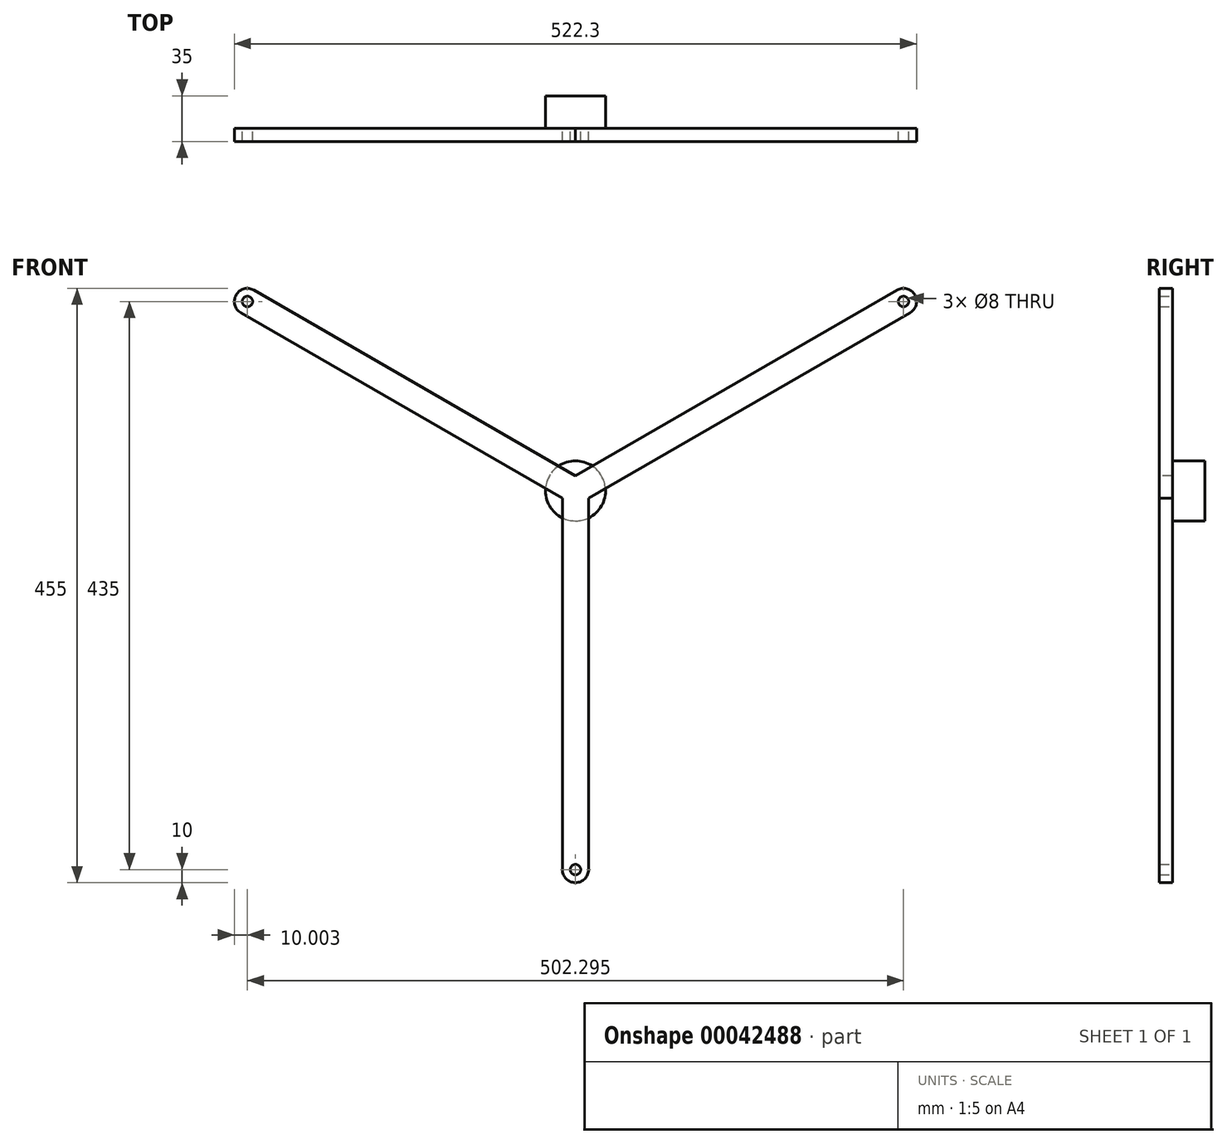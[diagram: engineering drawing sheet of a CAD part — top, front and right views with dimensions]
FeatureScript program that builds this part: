
annotation { "Feature Type Name" : "Feature", "Feature Type Description" : "" }
export const myFeature = defineFeature(function(context is Context, id is Id, definition is map)
    precondition{}
    {
        {
            var Q0;
            Q0=qCreatedBy(makeId("Front.planeOp"),FACE);
            var sketch = newSketch(context, id + "F0", { "sketchPlane" : qUnion([Q0])});
            skLineSegment(sketch, "E0.bottom", {"start": v(0, -300) * mm, "end": v(0, -300) * mm});
            skLineSegment(sketch, "E0.top", {"start": v(-10, 0) * mm, "end": v(10, 0) * mm});
            skLineSegment(sketch, "E0.left", {"start": v(-10, -290) * mm, "end": v(-10, 0) * mm});
            skLineSegment(sketch, "E0.right", {"start": v(10, -290) * mm, "end": v(10, 0) * mm});
            skCircle(sketch, "E1", {"center": v(0, -290) * mm, "radius": 4 * mm});
            skPoint(sketch, "E2.visualSharp", {"position": v(10, -300) * mm});
            skArc(sketch, "E2.filletArc", {"start": v(0, -300) * mm, "mid": v(7.07, -297.07) * mm, "end": v(10, -290) * mm});
            skPoint(sketch, "E3.visualSharp", {"position": v(-10, -300) * mm});
            skArc(sketch, "E3.filletArc", {"start": v(-10, -290) * mm, "mid": v(-7.07, -297.07) * mm, "end": v(0, -300) * mm});
            skSolve(sketch);
        }
        {
            var Q0;
            Q0 = qSketchRegion(id + "F0", true);
            extrude(context, id + "F1", {"entities" : qUnion([Q0]), "depth" : 10 * mm});
        }
        {
            var Q0;
            Q0=qCreatedBy(makeId("Right.planeOp"),FACE);
            var sketch = newSketch(context, id + "F2", { "sketchPlane" : qUnion([Q0])});
            skLineSegment(sketch, "E4", {"start": v(0, 0) * mm, "end": v(-67.82, 0) * mm, "construction": true});
            skSolve(sketch);
        }
        {
            var Q0;
            Q0=makeQuery(id+"F1.opExtrude","SWEPT_BODY",BODY,{"disambiguationData":[OSD([sQuery(id+"F0.wireOp",EDGE,"E0.top"),sQuery(id+"F0.wireOp",EDGE,"E0.left"),sQuery(id+"F0.wireOp",EDGE,"E0.right"),sQuery(id+"F0.wireOp",EDGE,"E1"),sQuery(id+"F0.wireOp",EDGE,"E2.filletArc"),sQuery(id+"F0.wireOp",EDGE,"E3.filletArc")])]});
            var Q1;
            Q1=sQuery(id+"F2.wireOp",EDGE,"E4");
            circularPattern(context, id + "F3", {"entities" : qUnion([Q0]), "axis" : qUnion([Q1]), "angle" : 120 * degree, "instanceCount" : 3});
        }
        {
            var Q0;
            Q0=makeQuery(id+"F1.opExtrude","CAP_FACE",FACE,{"disambiguationData":[OSD([sQuery(id+"F0.wireOp",EDGE,"E0.top"),sQuery(id+"F0.wireOp",EDGE,"E0.left"),sQuery(id+"F0.wireOp",EDGE,"E0.right"),sQuery(id+"F0.wireOp",EDGE,"E1"),sQuery(id+"F0.wireOp",EDGE,"E2.filletArc"),sQuery(id+"F0.wireOp",EDGE,"E3.filletArc")])],"isStart":true});
            var sketch = newSketch(context, id + "F4", { "sketchPlane" : qUnion([Q0])});
            skCircle(sketch, "E5", {"center": v(0, 0) * mm, "radius": 23 * mm});
            skSolve(sketch);
        }
        {
            var Q0;
            Q0 = qSketchRegion(id + "F4", true);
            extrude(context, id + "F5", {"entities" : qUnion([Q0]), "operationType" : NewBodyOperationType.ADD, "depth" : 25 * mm});
        }
    });
